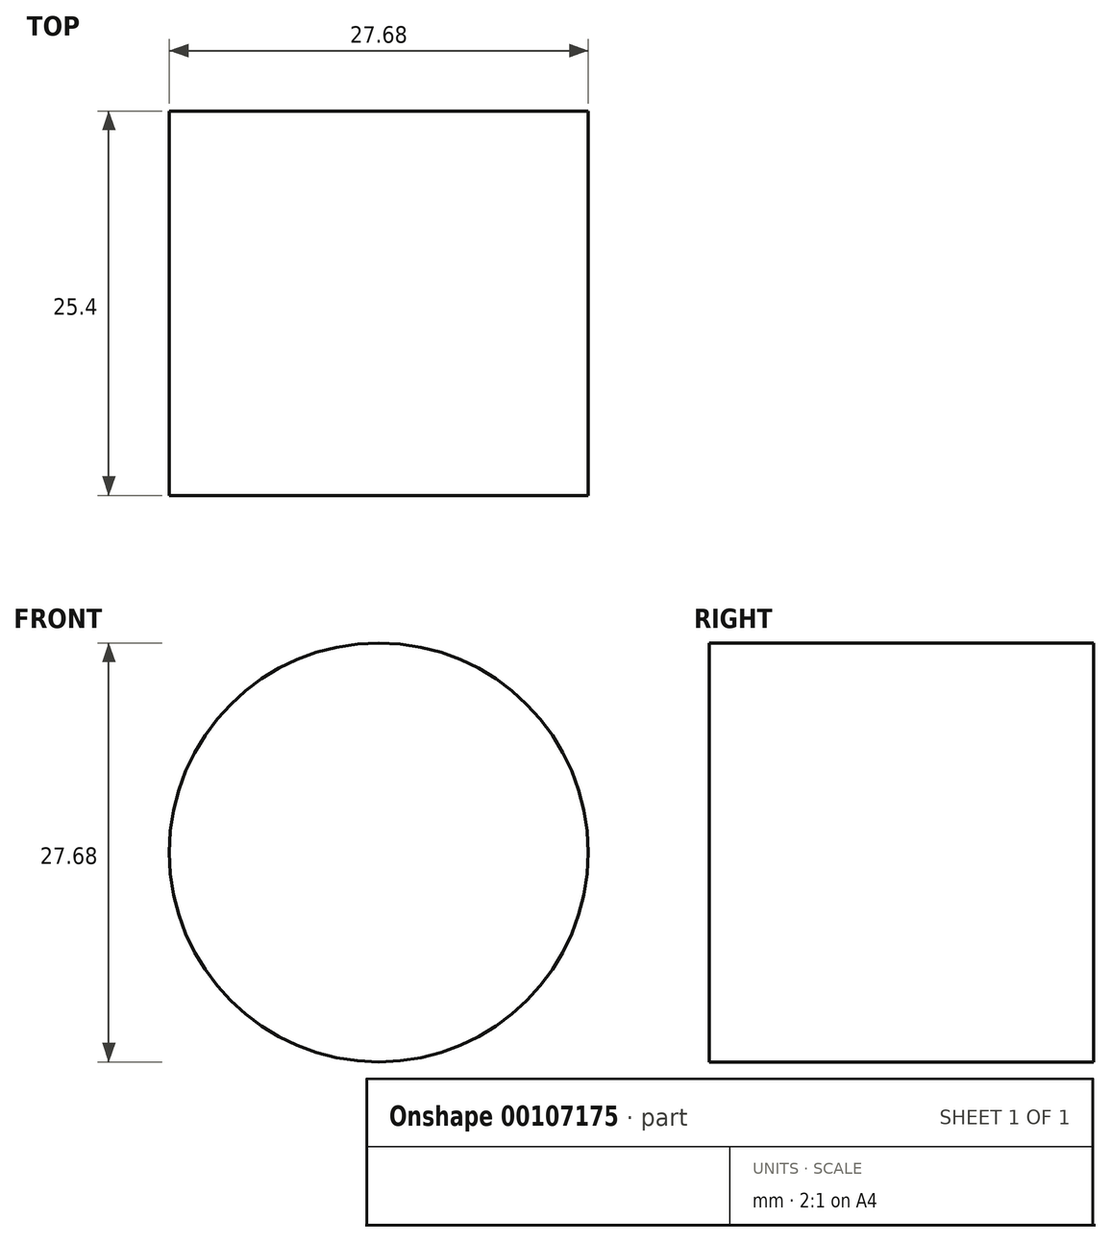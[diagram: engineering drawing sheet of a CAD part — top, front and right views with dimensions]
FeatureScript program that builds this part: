
annotation { "Feature Type Name" : "Feature", "Feature Type Description" : "" }
export const myFeature = defineFeature(function(context is Context, id is Id, definition is map)
    precondition{}
    {
        {
            var Q0;
            Q0=qCreatedBy(makeId("Front.planeOp"),FACE);
            var sketch = newSketch(context, id + "F0", { "sketchPlane" : qUnion([Q0])});
            skCircle(sketch, "E0", {"center": v(-122.45, -18.4) * mm, "radius": 19.95 * mm});
            skCircle(sketch, "E1", {"center": v(122.26, 34.8) * mm, "radius": 13.84 * mm});
            skCircle(sketch, "E2", {"center": v(-126.45, 32.7) * mm, "radius": 23.4 * mm});
            skCircle(sketch, "E3", {"center": v(-127.6, 18.21) * mm, "radius": 17.03 * mm});
            skCircle(sketch, "E4", {"center": v(-127.6, 18.21) * mm, "radius": 0.95 * mm});
            skSolve(sketch);
        }
        {
            var Q0;
            Q0=makeQuery(id+"F0.imprint","IMPRINT",FACE,{"disambiguationData":[TD([[makeQuery(id+"F0.imprint","IMPRINT",EDGE,{"derivedFrom":sQuery(id+"F0.wireOp",EDGE,"E1")}),1.0]])]});
            extrude(context, id + "F1", {"entities" : qUnion([Q0]), "depth" : 25.4 * mm});
        }
    });
